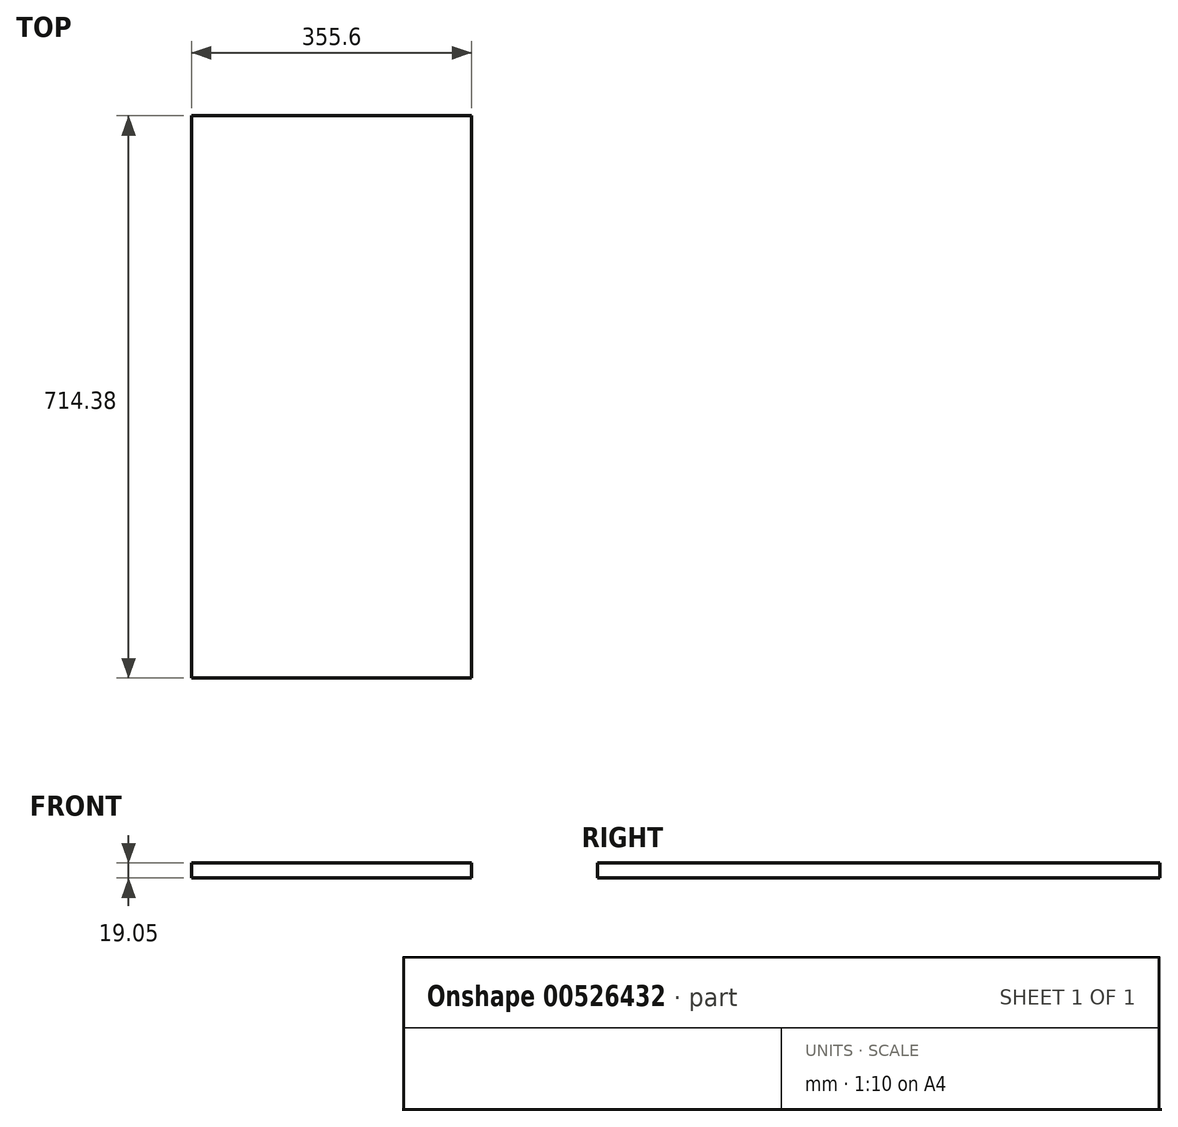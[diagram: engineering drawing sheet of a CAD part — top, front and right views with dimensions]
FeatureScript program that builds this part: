
annotation { "Feature Type Name" : "Feature", "Feature Type Description" : "" }
export const myFeature = defineFeature(function(context is Context, id is Id, definition is map)
    precondition{}
    {
        {
            var Q0;
            Q0=qCreatedBy(makeId("Top.planeOp"),FACE);
            var sketch = newSketch(context, id + "F0", { "sketchPlane" : qUnion([Q0])});
            skLineSegment(sketch, "E0.bottom", {"start": v(177.8, 357.19) * mm, "end": v(-177.8, 357.19) * mm});
            skLineSegment(sketch, "E0.top", {"start": v(177.8, -357.19) * mm, "end": v(-177.8, -357.19) * mm});
            skLineSegment(sketch, "E0.left", {"start": v(177.8, 357.19) * mm, "end": v(177.8, -357.19) * mm});
            skLineSegment(sketch, "E0.right", {"start": v(-177.8, 357.19) * mm, "end": v(-177.8, -357.19) * mm});
            skPoint(sketch, "E0.middle", {"position": v(0, 0) * mm});
            skSolve(sketch);
        }
        {
            var Q0;
            Q0=makeQuery(id+"F0.imprint","IMPRINT",FACE,{"disambiguationData":[TD([[makeQuery(id+"F0.imprint","IMPRINT",EDGE,{"derivedFrom":sQuery(id+"F0.wireOp",EDGE,"E0.bottom")}),1.0]])]});
            extrude(context, id + "F1", {"entities" : qUnion([Q0]), "depth" : 19.05 * mm, "offsetDistance" : 25.4 * mm});
        }
    });
